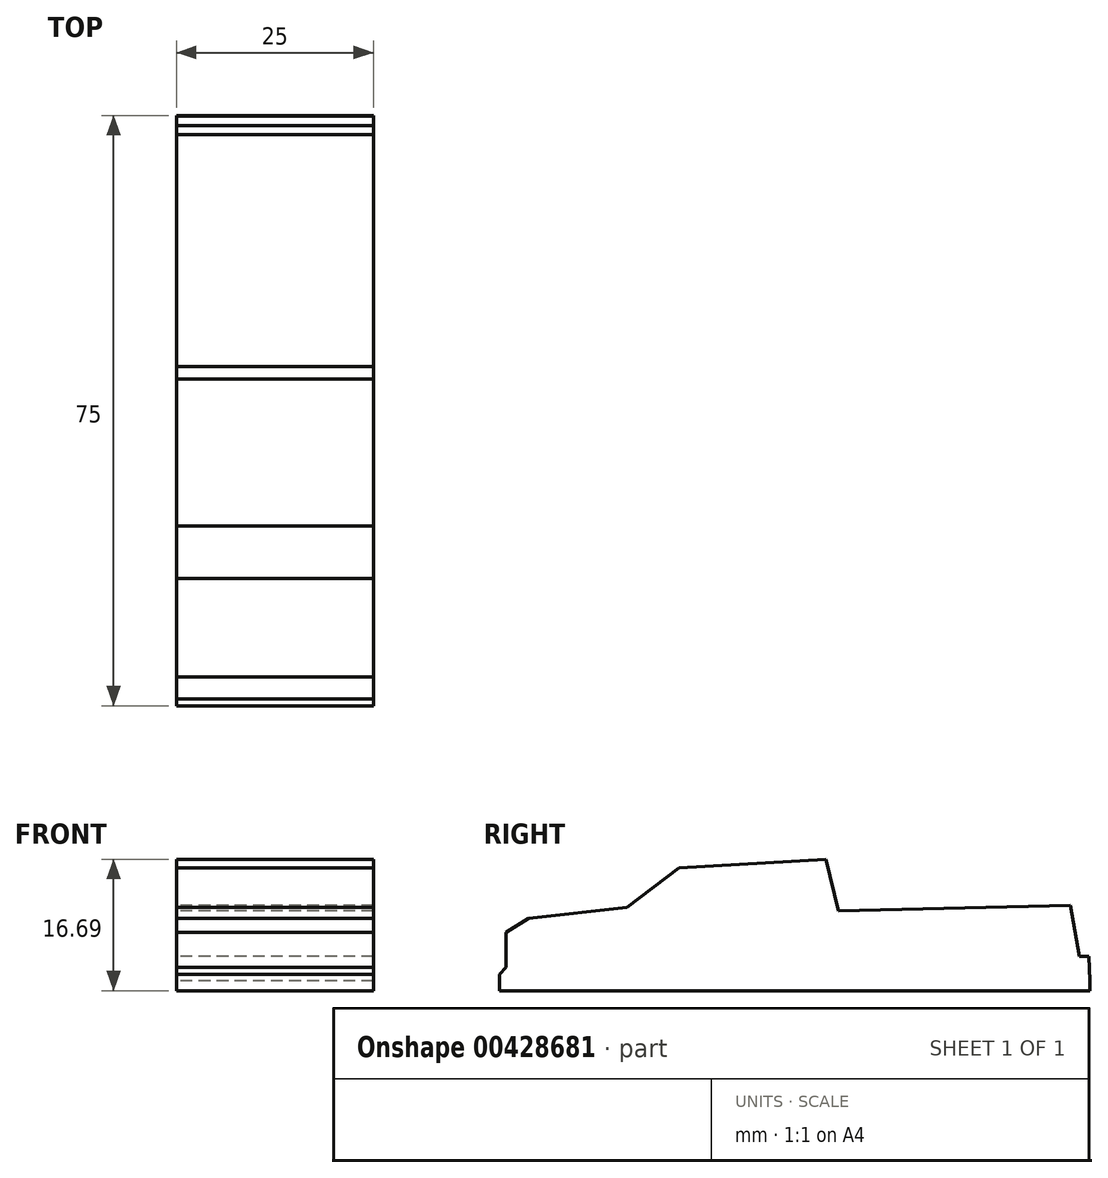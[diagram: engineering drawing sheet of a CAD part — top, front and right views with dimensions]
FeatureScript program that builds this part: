
annotation { "Feature Type Name" : "Feature", "Feature Type Description" : "" }
export const myFeature = defineFeature(function(context is Context, id is Id, definition is map)
    precondition{}
    {
        {
            var Q0;
            Q0=qCreatedBy(makeId("Right.planeOp"),FACE);
            var sketch = newSketch(context, id + "F0", { "sketchPlane" : qUnion([Q0])});
            skLineSegment(sketch, "E0", {"start": v(-41.48, 2.43) * mm, "end": v(33.52, 2.43) * mm});
            skLineSegment(sketch, "E1", {"start": v(-41.48, 2.43) * mm, "end": v(-41.48, 4.5) * mm});
            skLineSegment(sketch, "E2", {"start": v(-41.48, 4.5) * mm, "end": v(-40.6, 5.37) * mm});
            skLineSegment(sketch, "E3", {"start": v(-40.6, 9.84) * mm, "end": v(-37.79, 11.58) * mm});
            skLineSegment(sketch, "E4", {"start": v(-37.79, 11.58) * mm, "end": v(-25.29, 13) * mm});
            skLineSegment(sketch, "E5", {"start": v(-25.29, 13) * mm, "end": v(-18.66, 18.04) * mm});
            skLineSegment(sketch, "E6", {"start": v(-18.66, 18.04) * mm, "end": v(0, 19.12) * mm});
            skLineSegment(sketch, "E7", {"start": v(0, 19.12) * mm, "end": v(1.62, 12.58) * mm});
            skLineSegment(sketch, "E8", {"start": v(1.62, 12.58) * mm, "end": v(31.1, 13.24) * mm});
            skLineSegment(sketch, "E9", {"start": v(31.1, 13.24) * mm, "end": v(32.2, 6.76) * mm});
            skLineSegment(sketch, "E10", {"start": v(32.2, 6.76) * mm, "end": v(33.4, 6.79) * mm});
            skLineSegment(sketch, "E11", {"start": v(33.4, 6.79) * mm, "end": v(33.52, 3.67) * mm});
            skLineSegment(sketch, "E12", {"start": v(33.52, 3.67) * mm, "end": v(33.52, 2.43) * mm});
            skLineSegment(sketch, "E13", {"start": v(-40.6, 9.84) * mm, "end": v(-40.6, 5.37) * mm});
            skSolve(sketch);
        }
        {
            var Q0;
            Q0 = qSketchRegion(id + "F0", true);
            extrude(context, id + "F1", {"entities" : qUnion([Q0]), "depth" : 25 * mm});
        }
    });
